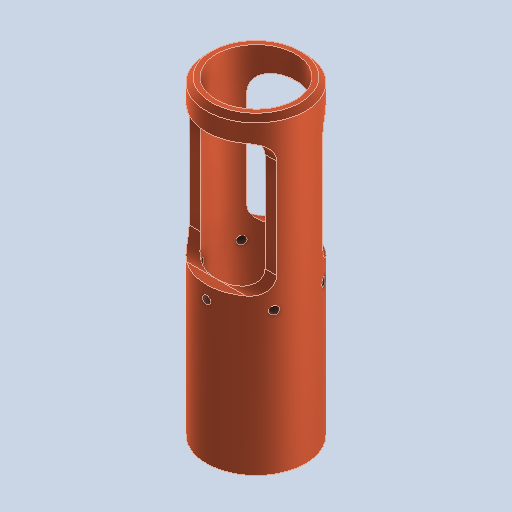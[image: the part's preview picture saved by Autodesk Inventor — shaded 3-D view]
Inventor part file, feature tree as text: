
AUTODESK INVENTOR PART (.ipt)
format: ipt  version: 2025.1 (Build 291241000, 241)  size: 349,696 bytes
history: native  units: mm
features: sketch x3, extrude x2, plane x2, hole x2, mirror x1, chamfer x1, fillet x1, pattern_circular x1
ambient origin geometry x8: Origin, YZ Plane, XZ Plane, XY Plane, X Axis, Y Axis, Z Axis, Center Point
bodies: Solid1 (feature_tree)
feature tree (13):
  extrude  "Extrusion1"  Depth=24.0mm
  plane  "Work Plane1"
  extrude  "Extrusion2"  Depth=15.0mm
  mirror  "Mirror1"
  chamfer  "Chamfer1"  Distance=7.0mm
  fillet  "Fillet1"  Radius=8.0mm
  plane  "Work Plane2"
  sketch  "Sketch3"  dims[d5=40.0mm d6=7.0mm d8=8.0mm d9=30.0mm d10=0.0mm d11=1.5mm d12=2.0mm d13=45.0deg d14=5.0mm d15=15.0mm d16=3.0mm d17=34.0mm d18=43.0mm d19=4.5mm d20=10.0mm d21=4.0mm d22=2.0mm d23=90.0deg d24=4.0mm d25=0.0mm d26=2.459mm d27=6.0mm d28=4.0mm d29=2.0mm d30=90.0deg d31=8.8mm d32=0.0mm d33=60.0mm d34=360.0deg]
  hole  "Hole1"  [1 undecoded]
  hole  "Hole2"  [1 undecoded]
  pattern_circular  "Circular Pattern1"  [2 undecoded]
  sketch  "Sketch1"  dims[d0=30.0mm d1=24.0mm]
  sketch  "Sketch2"  dims[d2=94.0mm d3=0.0mm d4=15.0mm]
note: 4 required parameter values undecoded (feature->parameter linkage not recoverable at this tier; creation-order binding heuristic only, values carry confidence <= 0.55)
